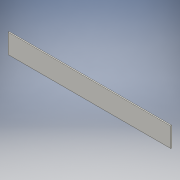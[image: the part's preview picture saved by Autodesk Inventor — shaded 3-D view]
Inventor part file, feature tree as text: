
AUTODESK INVENTOR PART (.ipt)
format: ipt  version: 2018 (Build 220112000, 112)  size: 92,160 bytes
history: native  units: mm
features: extrude x1, sketch x1
ambient origin geometry x8: Origin, YZ Plane, XZ Plane, XY Plane, X Axis, Y Axis, Z Axis, Center Point
bodies: Solid1 (feature_tree)
feature tree (2):
  extrude  "Extrusion1"  Depth=30.0mm
  sketch  "Sketch1"  dims[d0=250.0mm d1=30.0mm d2=1.6mm d3=0.0mm]
